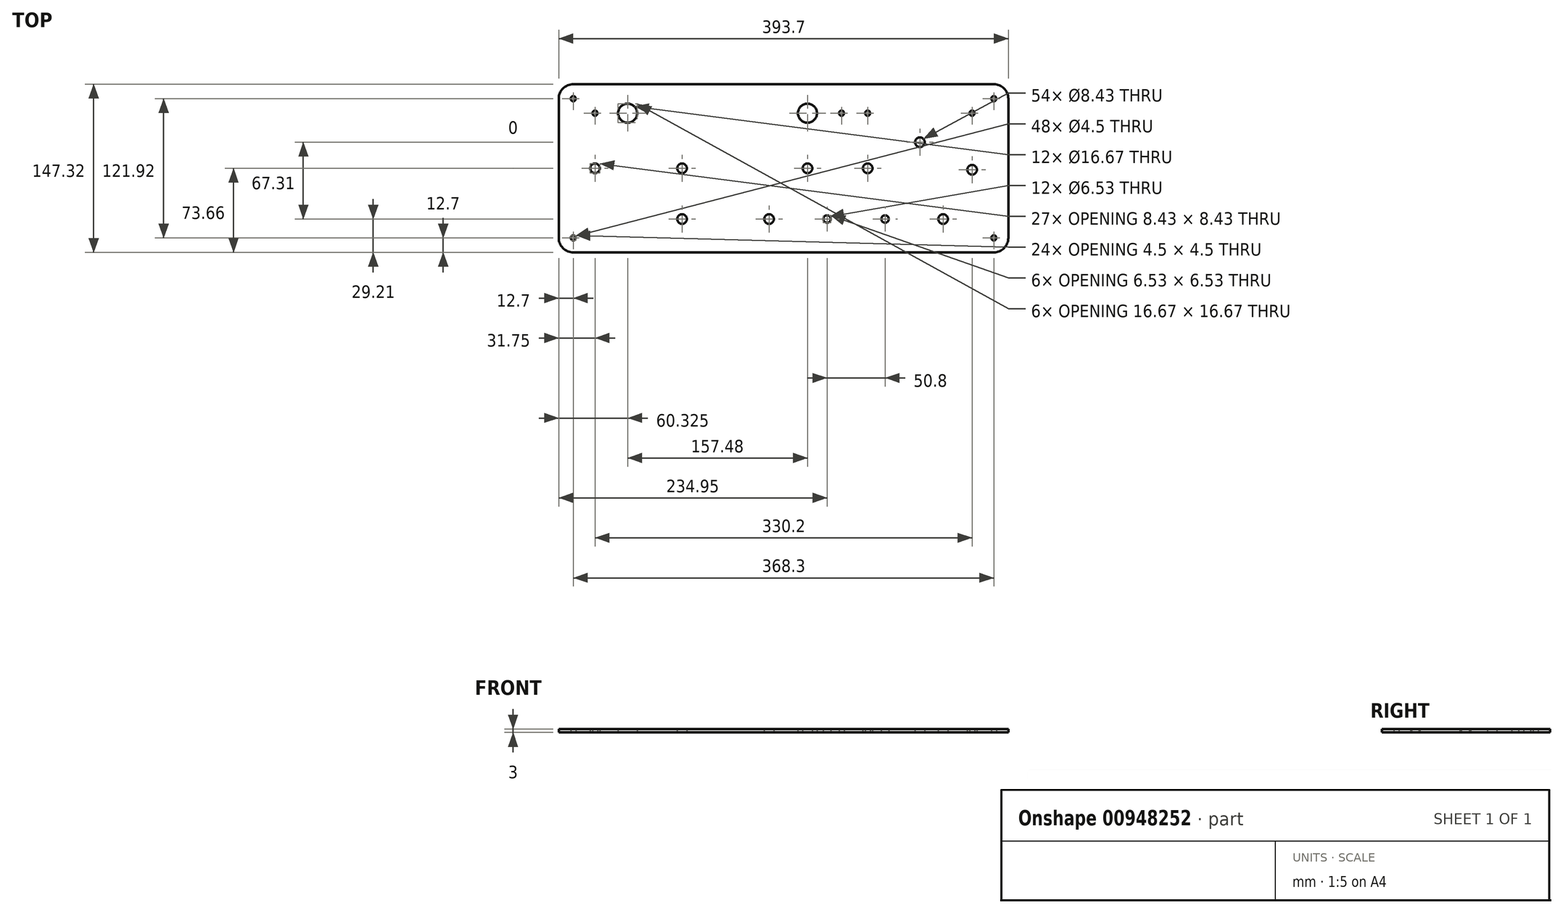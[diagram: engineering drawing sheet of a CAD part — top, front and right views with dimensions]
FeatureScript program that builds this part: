
annotation { "Feature Type Name" : "Feature", "Feature Type Description" : "" }
export const myFeature = defineFeature(function(context is Context, id is Id, definition is map)
    precondition{}
    {
        {
            var Q0;
            Q0=qCreatedBy(makeId("Top.planeOp"),FACE);
            var sketch = newSketch(context, id + "F0", { "sketchPlane" : qUnion([Q0])});
            skLineSegment(sketch, "E0.bottom", {"start": v(184.15, 73.66) * mm, "end": v(-184.15, 73.66) * mm});
            skLineSegment(sketch, "E0.top", {"start": v(184.15, -73.66) * mm, "end": v(-184.15, -73.66) * mm});
            skLineSegment(sketch, "E0.left", {"start": v(196.85, 60.96) * mm, "end": v(196.85, -60.96) * mm});
            skLineSegment(sketch, "E0.right", {"start": v(-196.85, 60.96) * mm, "end": v(-196.85, -60.96) * mm});
            skPoint(sketch, "E0.middle", {"position": v(0, 0) * mm});
            skPoint(sketch, "E1", {"position": v(-165.1, 48.26) * mm});
            skPoint(sketch, "E2", {"position": v(50.8, 48.26) * mm});
            skPoint(sketch, "E3", {"position": v(73.66, 48.26) * mm});
            skPoint(sketch, "E4", {"position": v(165.1, 48.26) * mm});
            skPoint(sketch, "E5", {"position": v(-136.53, 48.26) * mm});
            skPoint(sketch, "E6", {"position": v(20.95, 48.26) * mm});
            skPoint(sketch, "E7", {"position": v(-88.9, 0) * mm});
            skPoint(sketch, "E8", {"position": v(20.96, 0) * mm});
            skPoint(sketch, "E9", {"position": v(73.66, 0) * mm});
            skPoint(sketch, "E10", {"position": v(165.1, -1.27) * mm});
            skPoint(sketch, "E11", {"position": v(-165.1, 0) * mm});
            skPoint(sketch, "E12", {"position": v(-88.9, -44.45) * mm});
            skPoint(sketch, "E13", {"position": v(38.1, -44.45) * mm});
            skPoint(sketch, "E14", {"position": v(88.9, -44.45) * mm});
            skPoint(sketch, "E15", {"position": v(139.7, -44.45) * mm});
            skPoint(sketch, "E16", {"position": v(184.15, 60.96) * mm});
            skPoint(sketch, "E17", {"position": v(184.15, -60.96) * mm});
            skPoint(sketch, "E18", {"position": v(-184.15, -60.96) * mm});
            skPoint(sketch, "E19", {"position": v(-184.15, 60.96) * mm});
            skPoint(sketch, "E20", {"position": v(119.38, 22.86) * mm});
            skPoint(sketch, "E21.visualSharp", {"position": v(-196.85, 73.66) * mm});
            skArc(sketch, "E21.filletArc", {"start": v(-184.15, 73.66) * mm, "mid": v(-193.13, 69.94) * mm, "end": v(-196.85, 60.96) * mm});
            skPoint(sketch, "E22.visualSharp", {"position": v(196.85, 73.66) * mm});
            skArc(sketch, "E22.filletArc", {"start": v(196.85, 60.96) * mm, "mid": v(193.13, 69.94) * mm, "end": v(184.15, 73.66) * mm});
            skPoint(sketch, "E23.visualSharp", {"position": v(196.85, -73.66) * mm});
            skArc(sketch, "E23.filletArc", {"start": v(184.15, -73.66) * mm, "mid": v(193.13, -69.94) * mm, "end": v(196.85, -60.96) * mm});
            skPoint(sketch, "E24.visualSharp", {"position": v(-196.85, -73.66) * mm});
            skArc(sketch, "E24.filletArc", {"start": v(-196.85, -60.96) * mm, "mid": v(-193.13, -69.94) * mm, "end": v(-184.15, -73.66) * mm});
            skPoint(sketch, "E25", {"position": v(-12.7, -44.45) * mm});
            skSolve(sketch);
        }
        {
            var Q0;
            Q0=qSketchRegion(id+"F0",true);
            extrude(context, id + "F1", {"entities" : qUnion([Q0]), "depth" : 3 * mm, "offsetDistance" : 25.4 * mm});
        }
        {
            var Q0;
            Q0=sQuery(id+"F0.wireOp",VERTEX,"E4");
            var Q1;
            Q1=sQuery(id+"F0.wireOp",VERTEX,"E3");
            var Q2;
            Q2=sQuery(id+"F0.wireOp",VERTEX,"E2");
            var Q3;
            Q3=sQuery(id+"F0.wireOp",VERTEX,"E1");
            var Q4;
            Q4=sQuery(id+"F0.wireOp",VERTEX,"E19");
            var Q5;
            Q5=sQuery(id+"F0.wireOp",VERTEX,"E18");
            var Q6;
            Q6=sQuery(id+"F0.wireOp",VERTEX,"E17");
            var Q7;
            Q7=sQuery(id+"F0.wireOp",VERTEX,"E16");
            var Q8;
            Q8=makeQuery(id+"F1.opExtrude","SWEPT_BODY",BODY,{"disambiguationData":[OSD([sQuery(id+"F0.wireOp",EDGE,"E0.bottom"),sQuery(id+"F0.wireOp",EDGE,"E0.top"),sQuery(id+"F0.wireOp",EDGE,"E0.left"),sQuery(id+"F0.wireOp",EDGE,"E0.right")])]});
            hole(context, id + "F2", {"style" : HoleStyle.SIMPLE, "endStyle" : HoleEndStyle.THROUGH, "oppositeDirection" : true, "standardTappedOrClearance" : lookupTablePath({ "standard" : "ANSI", "fit" : "Normal (ASME)", "size" : "#8", "type" : "Clearance" }), "standardBlindInLast" : lookupTablePath({ "fit" : "Free", "standard" : "ANSI", "size" : "#8", "type" : "Clearance" }), "holeDiameter" : 4.5 * mm, "majorDiameter" : 6.35 * mm, "isTappedThrough" : true, "tappedDepth" : 12.7 * mm, "tapClearance" : 3, "locations" : qUnion([Q0, Q1, Q2, Q3, Q4, Q5, Q6, Q7]), "scope" : qUnion([Q8])});
        }
        {
            var Q0;
            Q0=sQuery(id+"F0.wireOp",VERTEX,"E6");
            var Q1;
            Q1=sQuery(id+"F0.wireOp",VERTEX,"E5");
            var Q2;
            Q2=makeQuery(id+"F1.opExtrude","SWEPT_BODY",BODY,{"disambiguationData":[OSD([sQuery(id+"F0.wireOp",EDGE,"E0.bottom"),sQuery(id+"F0.wireOp",EDGE,"E0.top"),sQuery(id+"F0.wireOp",EDGE,"E0.left"),sQuery(id+"F0.wireOp",EDGE,"E0.right")])]});
            hole(context, id + "F3", {"style" : HoleStyle.SIMPLE, "endStyle" : HoleEndStyle.THROUGH, "oppositeDirection" : true, "standardTappedOrClearance" : lookupTablePath({ "standard" : "ANSI", "fit" : "Normal (ASME)", "size" : "5/8", "type" : "Clearance" }), "standardBlindInLast" : lookupTablePath({ "fit" : "Free", "standard" : "ANSI", "size" : "5/8", "type" : "Clearance" }), "holeDiameter" : 16.67 * mm, "majorDiameter" : 6.35 * mm, "isTappedThrough" : true, "tappedDepth" : 12.7 * mm, "tapClearance" : 3, "locations" : qUnion([Q0, Q1]), "scope" : qUnion([Q2])});
        }
        {
            var Q0;
            Q0=sQuery(id+"F0.wireOp",VERTEX,"E10");
            var Q1;
            Q1=sQuery(id+"F0.wireOp",VERTEX,"E9");
            var Q2;
            Q2=sQuery(id+"F0.wireOp",VERTEX,"E8");
            var Q3;
            Q3=sQuery(id+"F0.wireOp",VERTEX,"E7");
            var Q4;
            Q4=sQuery(id+"F0.wireOp",VERTEX,"E15");
            var Q5;
            Q5=sQuery(id+"F0.wireOp",VERTEX,"E12");
            var Q6;
            Q6=sQuery(id+"F0.wireOp",VERTEX,"E11");
            var Q7;
            Q7=sQuery(id+"F0.wireOp",VERTEX,"E20");
            var Q8;
            Q8=sQuery(id+"F0.wireOp",VERTEX,"E25");
            var Q9;
            Q9=makeQuery(id+"F1.opExtrude","SWEPT_BODY",BODY,{"disambiguationData":[OSD([sQuery(id+"F0.wireOp",EDGE,"E0.bottom"),sQuery(id+"F0.wireOp",EDGE,"E0.top"),sQuery(id+"F0.wireOp",EDGE,"E0.left"),sQuery(id+"F0.wireOp",EDGE,"E0.right")])]});
            hole(context, id + "F4", {"style" : HoleStyle.SIMPLE, "endStyle" : HoleEndStyle.THROUGH, "oppositeDirection" : true, "standardTappedOrClearance" : lookupTablePath({ "standard" : "ANSI", "fit" : "Normal (ASME)", "size" : "5/16", "type" : "Clearance" }), "standardBlindInLast" : lookupTablePath({ "fit" : "Free", "standard" : "ANSI", "size" : "5/16", "type" : "Clearance" }), "holeDiameter" : 8.43 * mm, "majorDiameter" : 6.35 * mm, "isTappedThrough" : true, "tappedDepth" : 12.7 * mm, "tapClearance" : 3, "locations" : qUnion([Q0, Q1, Q2, Q3, Q4, Q5, Q6, Q7, Q8]), "scope" : qUnion([Q9])});
        }
        {
            var Q0;
            Q0=sQuery(id+"F0.wireOp",VERTEX,"E13");
            var Q1;
            Q1=sQuery(id+"F0.wireOp",VERTEX,"E14");
            var Q2;
            Q2=makeQuery(id+"F1.opExtrude","SWEPT_BODY",BODY,{"disambiguationData":[OSD([sQuery(id+"F0.wireOp",EDGE,"E0.bottom"),sQuery(id+"F0.wireOp",EDGE,"E0.top"),sQuery(id+"F0.wireOp",EDGE,"E0.left"),sQuery(id+"F0.wireOp",EDGE,"E0.right")])]});
            hole(context, id + "F5", {"style" : HoleStyle.SIMPLE, "endStyle" : HoleEndStyle.THROUGH, "oppositeDirection" : true, "standardTappedOrClearance" : lookupTablePath({ "standard" : "ANSI", "fit" : "Close", "size" : "1/4", "type" : "Clearance" }), "standardBlindInLast" : lookupTablePath({ "fit" : "Close", "standard" : "ANSI", "size" : "1/4", "type" : "Clearance" }), "holeDiameter" : 6.53 * mm, "majorDiameter" : 6.35 * mm, "isTappedThrough" : true, "tappedDepth" : 12.7 * mm, "tapClearance" : 3, "locations" : qUnion([Q0, Q1]), "scope" : qUnion([Q2])});
        }
    });
